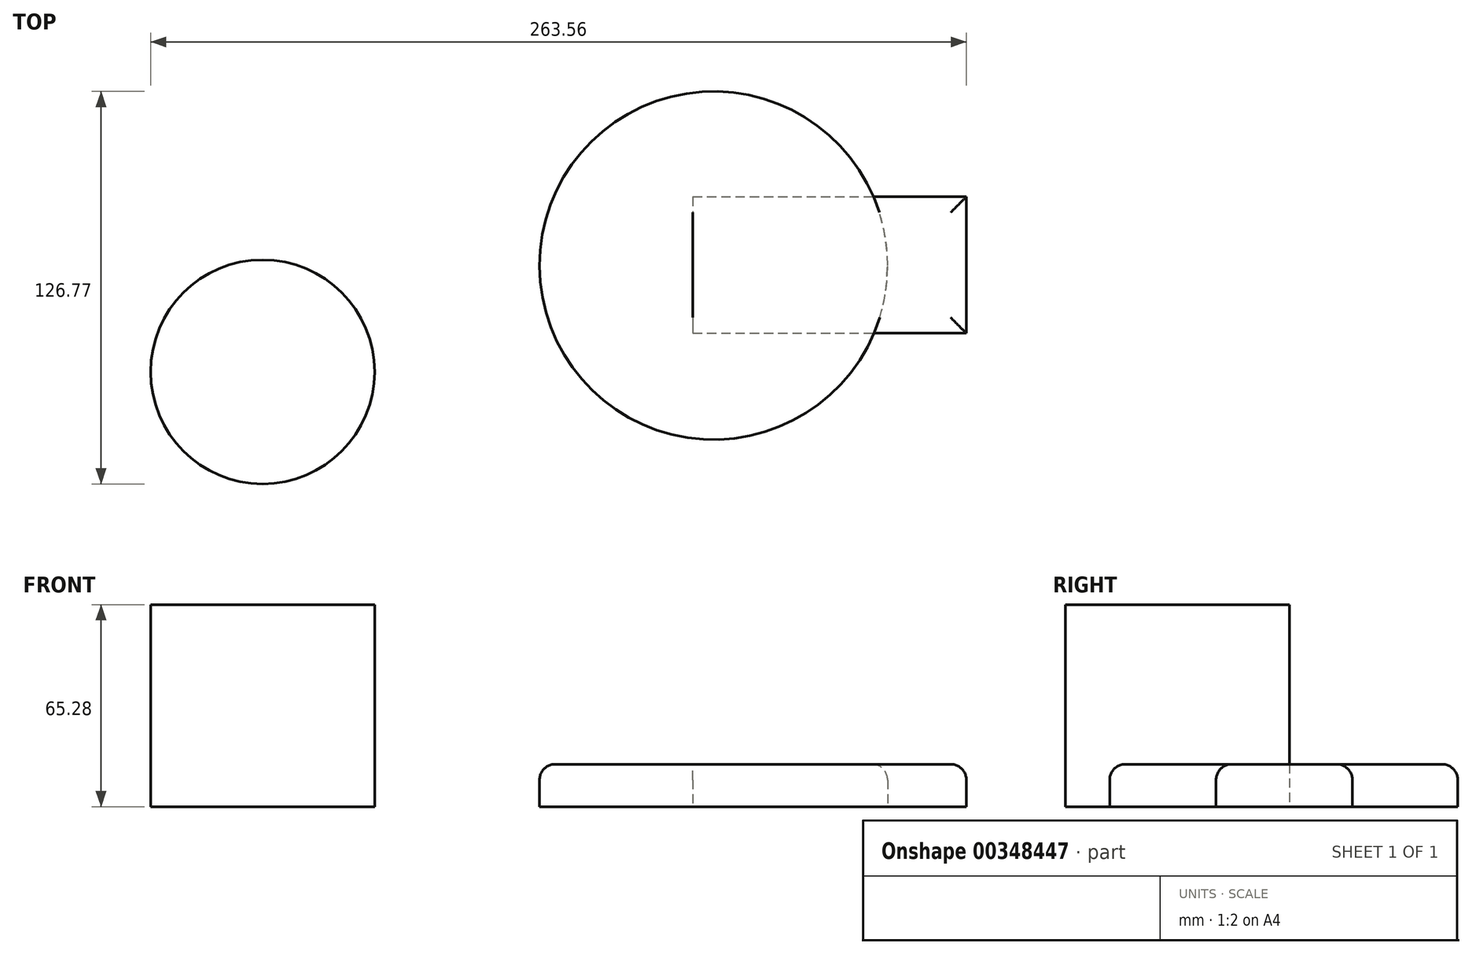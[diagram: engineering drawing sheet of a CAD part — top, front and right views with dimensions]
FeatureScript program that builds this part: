
annotation { "Feature Type Name" : "Feature", "Feature Type Description" : "" }
export const myFeature = defineFeature(function(context is Context, id is Id, definition is map)
    precondition{}
    {
        {
            var Q0;
            Q0=qCreatedBy(makeId("Top.planeOp"),FACE);
            var sketch = newSketch(context, id + "F0", { "sketchPlane" : qUnion([Q0])});
            skCircle(sketch, "E0", {"center": v(1.77, 0) * mm, "radius": 56.23 * mm});
            skSolve(sketch);
        }
        {
            var Q0;
            Q0=qCreatedBy(makeId("Top.planeOp"),FACE);
            var sketch = newSketch(context, id + "F1", { "sketchPlane" : qUnion([Q0])});
            skLineSegment(sketch, "E1.bottom", {"start": v(-4.95, 22.19) * mm, "end": v(83.44, 22.19) * mm});
            skLineSegment(sketch, "E1.top", {"start": v(-4.95, -21.87) * mm, "end": v(83.44, -21.87) * mm});
            skLineSegment(sketch, "E1.left", {"start": v(-4.95, 22.19) * mm, "end": v(-4.95, -21.87) * mm});
            skLineSegment(sketch, "E1.right", {"start": v(83.44, 22.19) * mm, "end": v(83.44, -21.87) * mm});
            skSolve(sketch);
        }
        {
            var Q0;
            Q0=makeQuery(id+"F0.imprint","IMPRINT",FACE,{"disambiguationData":[TD([[makeQuery(id+"F0.imprint","IMPRINT",EDGE,{"derivedFrom":sQuery(id+"F0.wireOp",EDGE,"E0")}),1.0]])]});
            var Q1;
            Q1=makeQuery(id+"F1.imprint","IMPRINT",FACE,{"disambiguationData":[TD([[makeQuery(id+"F1.imprint","IMPRINT",EDGE,{"derivedFrom":sQuery(id+"F1.wireOp",EDGE,"E1.bottom")}),-1.0]])]});
            extrude(context, id + "F2", {"entities" : qUnion([Q0, Q1]), "depth" : 13.72 * mm});
        }
        {
            var Q0;
            Q0=makeQuery(id+"F2.opExtrude","CAP_FACE",FACE,{"disambiguationData":[OSD([sQuery(id+"F0.wireOp",EDGE,"E0")])],"isStart":false});
            var Q1;
            Q1=makeQuery(id+"F2.opExtrude","CAP_EDGE",EDGE,{"disambiguationData":[OSD([sQuery(id+"F1.wireOp",EDGE,"E1.right")])],"isStart":false});
            var Q2;
            Q2=makeQuery(id+"F2.opExtrude","CAP_EDGE",EDGE,{"disambiguationData":[OSD([sQuery(id+"F1.wireOp",EDGE,"E1.top")])],"isStart":false});
            var Q3;
            Q3=makeQuery(id+"F2.opExtrude","CAP_EDGE",EDGE,{"disambiguationData":[OSD([sQuery(id+"F1.wireOp",EDGE,"E1.bottom")])],"isStart":false});
            fillet(context, id + "F3", {"entities" : qUnion([Q0, Q1, Q2, Q3]), "radius" : 5.08 * mm, "tangentPropagation" : true, "allowEdgeOverflow" : false});
        }
        {
            var Q0;
            Q0=qCreatedBy(makeId("Top.planeOp"),FACE);
            var sketch = newSketch(context, id + "F4", { "sketchPlane" : qUnion([Q0])});
            skCircle(sketch, "E2", {"center": v(-143.94, -34.36) * mm, "radius": 36.18 * mm});
            skSolve(sketch);
        }
        {
            var Q0;
            Q0=makeQuery(id+"F4.imprint","IMPRINT",FACE,{"disambiguationData":[TD([[makeQuery(id+"F4.imprint","IMPRINT",EDGE,{"derivedFrom":sQuery(id+"F4.wireOp",EDGE,"E2")}),1.0]])]});
            extrude(context, id + "F5", {"entities" : qUnion([Q0]), "depth" : 65.28 * mm});
        }
    });
